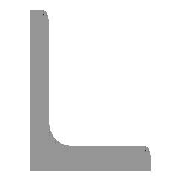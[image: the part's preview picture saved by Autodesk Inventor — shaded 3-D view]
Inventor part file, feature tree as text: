
AUTODESK INVENTOR PART (.ipt)
format: ipt  version: 2013 (Build 170138000, 138)  size: 128,512 bytes
history: native  units: mm (DEFAULTED — no unit token found)
features: other x4, plane x3, split x2, sketch x2
ambient origin geometry x8: Origin, YZ Plane, XZ Plane, XY Plane, X Axis, Y Axis, Z Axis, Center Point
bodies: Solid1 (feature_tree), Body (feature_tree)
feature tree (11):
  parser-record x1  (decoder bookkeeping rows leaked as tree rows — omitted from the tree; the rows remain in map.json)
  other  "Driven Length"
  other  "Start plane"
  other  "End plane"
  plane  "Work Plane4"
  split  "Split1"
  plane  "Work Plane5"
  split  "Split2"
  sketch  "Sketch3"  dims[d0=38.1mm]
  plane  "Work Plane3"
  sketch  "Sketch4"  dims[d1=38.1mm d2=4.7625mm d3=4.7625mm d4=1841.5mm d5=0.0mm d10=0.0mm d11=0.0mm d12=-0.0mm d13=1841.5mm d14=4.826mm d15=2.286mm d16=90.0deg d17=1841.5mm]
